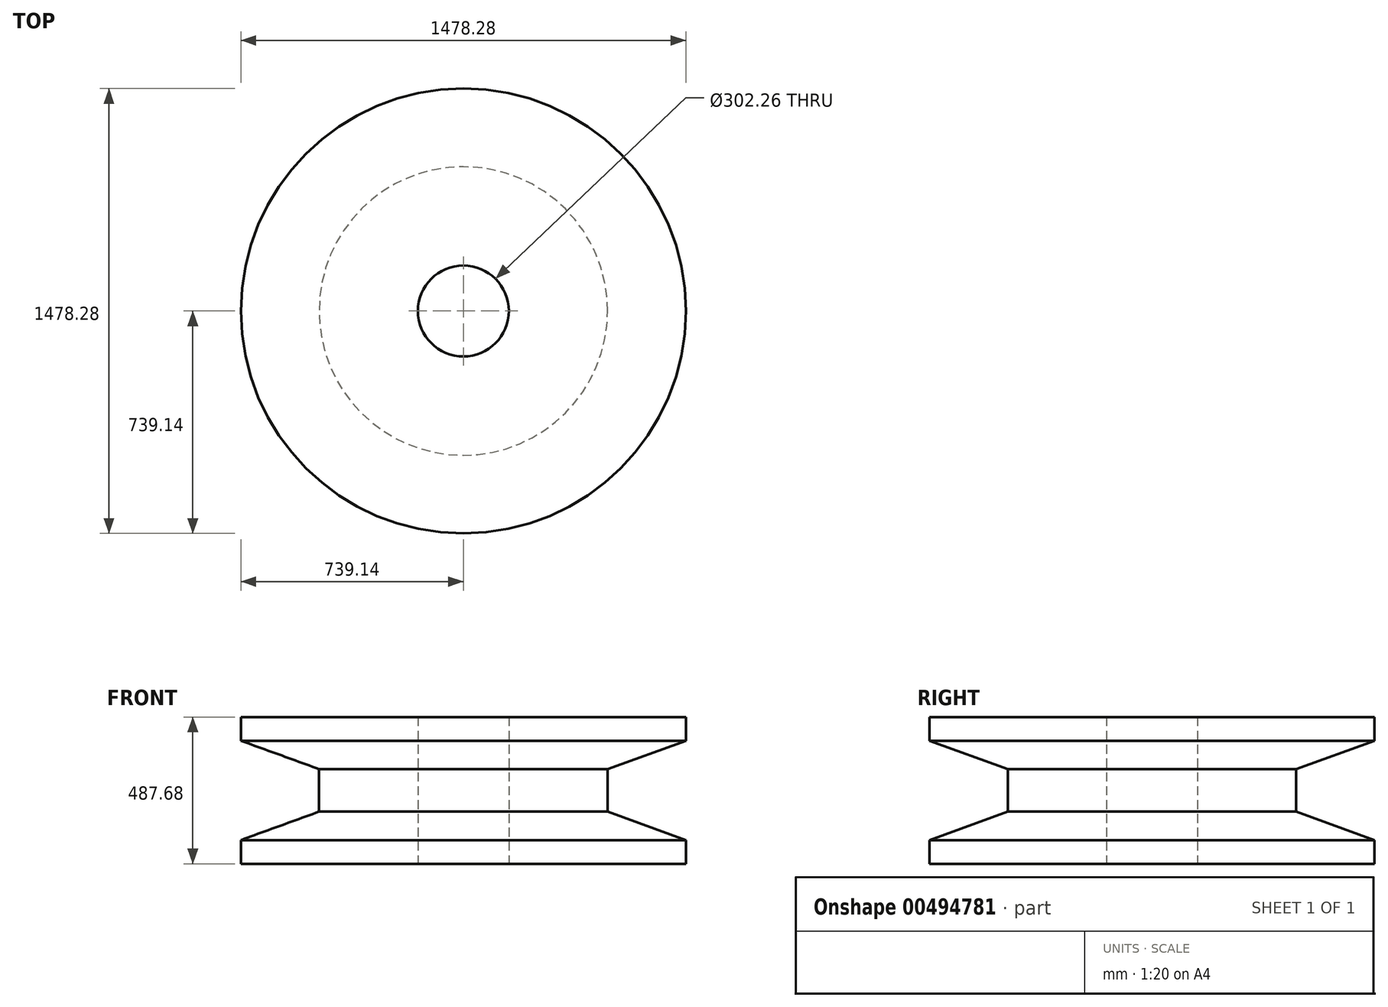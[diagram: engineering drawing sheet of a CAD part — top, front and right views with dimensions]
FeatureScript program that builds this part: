
annotation { "Feature Type Name" : "Feature", "Feature Type Description" : "" }
export const myFeature = defineFeature(function(context is Context, id is Id, definition is map)
    precondition{}
    {
        {
            var Q0;
            Q0=qCreatedBy(makeId("Front.planeOp"),FACE);
            var sketch = newSketch(context, id + "F0", { "sketchPlane" : qUnion([Q0])});
            skLineSegment(sketch, "E0", {"start": v(151.13, 0) * mm, "end": v(739.14, 0) * mm});
            skLineSegment(sketch, "E1", {"start": v(739.14, 0) * mm, "end": v(739.14, 78.74) * mm});
            skLineSegment(sketch, "E2", {"start": v(739.14, 78.74) * mm, "end": v(479.19, 173.36) * mm});
            skLineSegment(sketch, "E3", {"start": v(479.19, 173.36) * mm, "end": v(479.19, 314.33) * mm});
            skLineSegment(sketch, "E4", {"start": v(479.19, 314.33) * mm, "end": v(739.14, 408.94) * mm});
            skLineSegment(sketch, "E5", {"start": v(739.14, 408.94) * mm, "end": v(739.14, 487.68) * mm});
            skLineSegment(sketch, "E6", {"start": v(739.14, 487.68) * mm, "end": v(151.13, 487.68) * mm});
            skLineSegment(sketch, "E7", {"start": v(151.13, 487.68) * mm, "end": v(151.13, 0) * mm});
            skLineSegment(sketch, "E8", {"start": v(0, 0) * mm, "end": v(0, 487.68) * mm, "construction": true});
            skSolve(sketch);
        }
        {
            var Q0;
            Q0=makeQuery(id+"F0.imprint","IMPRINT",FACE,{"disambiguationData":[TD([[makeQuery(id+"F0.imprint","IMPRINT",EDGE,{"derivedFrom":sQuery(id+"F0.wireOp",EDGE,"E0")}),1.0]])]});
            var Q1;
            Q1=sQuery(id+"F0.wireOp",EDGE,"E8");
            revolve(context, id + "F1", {"entities" : qUnion([Q0]), "axis" : qUnion([Q1]), "revolveType" : RevolveType.FULL});
        }
    });
